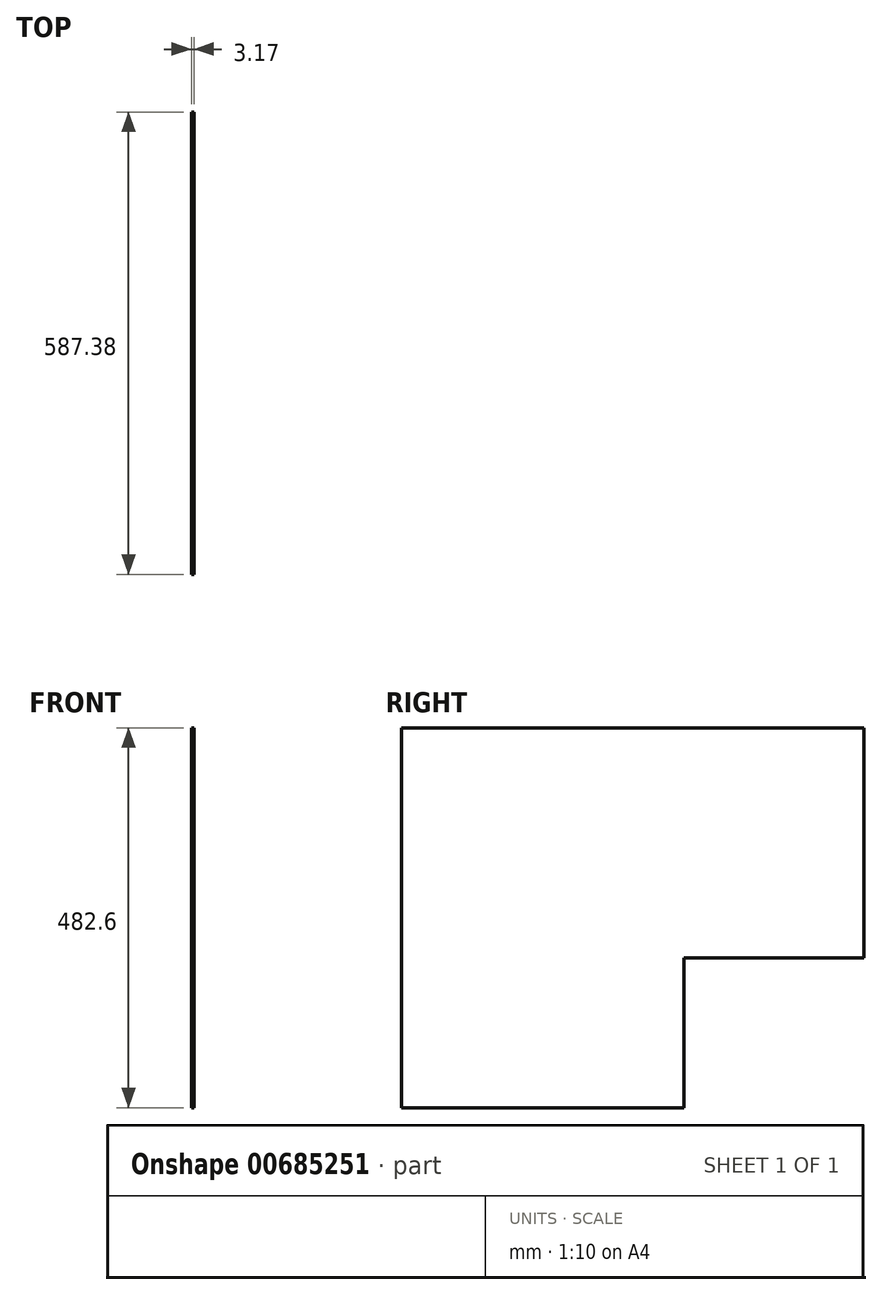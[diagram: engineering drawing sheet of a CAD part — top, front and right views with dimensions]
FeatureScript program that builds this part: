
annotation { "Feature Type Name" : "Feature", "Feature Type Description" : "" }
export const myFeature = defineFeature(function(context is Context, id is Id, definition is map)
    precondition{}
    {
        {
            var Q0;
            Q0=qCreatedBy(makeId("Right.planeOp"),FACE);
            var sketch = newSketch(context, id + "F0", { "sketchPlane" : qUnion([Q0])});
            skLineSegment(sketch, "E0.bottom", {"start": v(293.69, 241.3) * mm, "end": v(-293.69, 241.3) * mm});
            skLineSegment(sketch, "E0.top", {"start": v(65.09, -241.3) * mm, "end": v(-293.69, -241.3) * mm});
            skLineSegment(sketch, "E0.left", {"start": v(293.69, 241.3) * mm, "end": v(293.69, -50.8) * mm});
            skLineSegment(sketch, "E0.right", {"start": v(-293.69, 241.3) * mm, "end": v(-293.69, -241.3) * mm});
            skPoint(sketch, "E0.middle", {"position": v(0, 0) * mm});
            skLineSegment(sketch, "E1.top", {"start": v(293.69, -50.8) * mm, "end": v(65.09, -50.8) * mm});
            skLineSegment(sketch, "E1.right", {"start": v(65.09, -241.3) * mm, "end": v(65.09, -50.8) * mm});
            skPoint(sketch, "E2.orphan", {"position": v(293.69, -241.3) * mm});
            skSolve(sketch);
        }
        {
            var Q0;
            Q0 = qSketchRegion(id + "F0", true);
            extrude(context, id + "F1", {"entities" : qUnion([Q0]), "depth" : 3.17 * mm, "offsetDistance" : 25.4 * mm});
        }
    });
